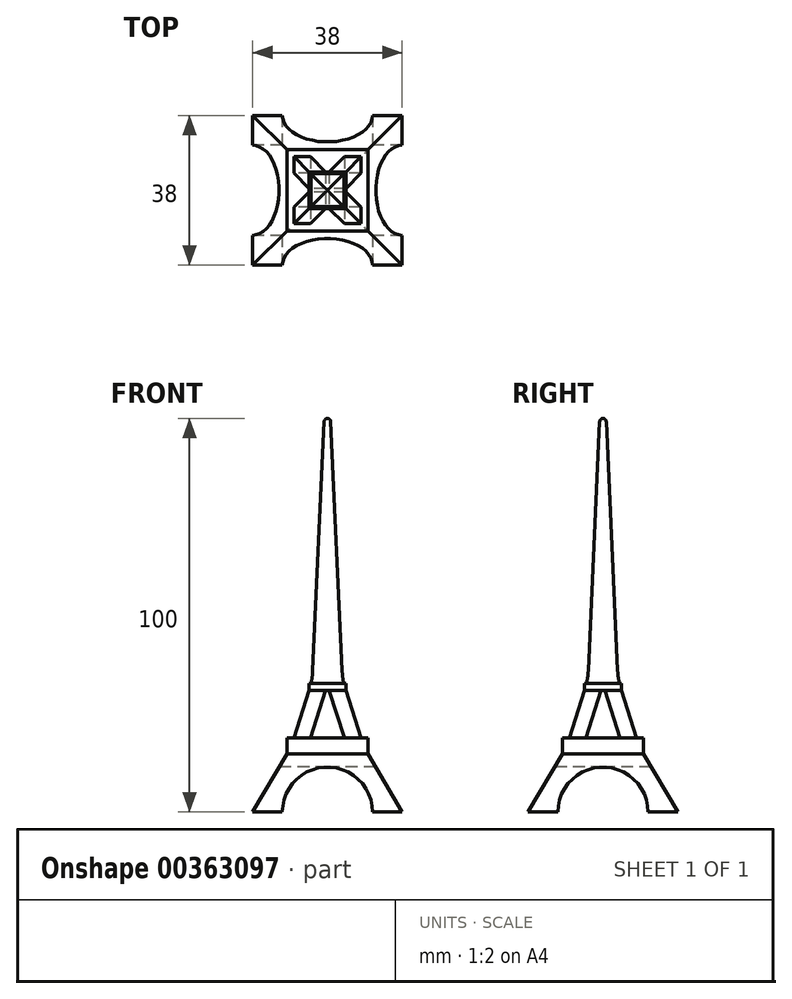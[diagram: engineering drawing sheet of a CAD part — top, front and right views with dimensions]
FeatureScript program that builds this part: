
annotation { "Feature Type Name" : "Feature", "Feature Type Description" : "" }
export const myFeature = defineFeature(function(context is Context, id is Id, definition is map)
    precondition{}
    {
        {
            var Q0;
            Q0=qCreatedBy(makeId("Front.planeOp"),FACE);
            var sketch = newSketch(context, id + "F0", { "sketchPlane" : qUnion([Q0])});
            skLineSegment(sketch, "E0.bottom", {"start": v(0, 0) * mm, "end": v(38, 0) * mm});
            skLineSegment(sketch, "E0.top", {"start": v(0, 100) * mm, "end": v(38, 100) * mm});
            skLineSegment(sketch, "E0.left", {"start": v(0, 0) * mm, "end": v(0, 100) * mm});
            skLineSegment(sketch, "E0.right", {"start": v(38, 0) * mm, "end": v(38, 100) * mm});
            skSolve(sketch);
        }
        {
            var Q0;
            Q0=makeQuery(id+"F0.imprint","IMPRINT",FACE,{"disambiguationData":[TD([[makeQuery(id+"F0.imprint","IMPRINT",EDGE,{"derivedFrom":sQuery(id+"F0.wireOp",EDGE,"E0.bottom")}),1.0]])]});
            extrude(context, id + "F1", {"entities" : qUnion([Q0]), "depth" : 38 * mm, "offsetDistance" : 25 * mm});
        }
        {
            var Q0;
            Q0=makeQuery(id+"F1.opExtrude","CAP_FACE",FACE,{"disambiguationData":[OSD([sQuery(id+"F0.wireOp",EDGE,"E0.bottom"),sQuery(id+"F0.wireOp",EDGE,"E0.top"),sQuery(id+"F0.wireOp",EDGE,"E0.left"),sQuery(id+"F0.wireOp",EDGE,"E0.right")])],"isStart":false});
            var sketch = newSketch(context, id + "F2", { "sketchPlane" : qUnion([Q0])});
            skPoint(sketch, "E1.endSnap0", {"position": v(19, 100) * mm});
            skLineSegment(sketch, "E2", {"start": v(19, 100) * mm, "end": v(19, 0) * mm, "construction": true});
            skLineSegment(sketch, "E3", {"start": v(19, 100) * mm, "end": v(19.03, 100) * mm});
            skLineSegment(sketch, "E4", {"start": v(19.83, 99.24) * mm, "end": v(22.72, 36.04) * mm});
            skLineSegment(sketch, "E5", {"start": v(38, 0) * mm, "end": v(29.32, 14.77) * mm});
            skLineSegment(sketch, "E6", {"start": v(27.53, 18.8) * mm, "end": v(23.66, 30.85) * mm});
            skArc(sketch, "E7", {"start": v(30.49, 0) * mm, "mid": v(27.12, 8.12) * mm, "end": v(19, 11.49) * mm});
            skLineSegment(sketch, "E8", {"start": v(38, 0) * mm, "end": v(30.49, 0) * mm});
            skPoint(sketch, "E9.visualSharp", {"position": v(22.85, 33.38) * mm});
            skArc(sketch, "E9.filletArc", {"start": v(22.72, 36.04) * mm, "mid": v(22.88, 34.33) * mm, "end": v(23.17, 32.64) * mm});
            skPoint(sketch, "E10.visualSharp", {"position": v(28.2, 16.68) * mm});
            skLineSegment(sketch, "E11.MirrorCS", {"start": v(18.17, 99.24) * mm, "end": v(15.28, 36.04) * mm});
            skArc(sketch, "E12.MirrorCS", {"start": v(15.28, 36.04) * mm, "mid": v(15.12, 34.33) * mm, "end": v(14.83, 32.64) * mm});
            skLineSegment(sketch, "E13.MirrorCS", {"start": v(10.47, 18.8) * mm, "end": v(14.34, 30.85) * mm});
            skLineSegment(sketch, "E14.MirrorCS", {"start": v(19, 100) * mm, "end": v(18.97, 100) * mm});
            skLineSegment(sketch, "E15.MirrorCS", {"start": v(0, 0) * mm, "end": v(8.68, 14.77) * mm});
            skArc(sketch, "E16.MirrorCS", {"start": v(7.51, 0) * mm, "mid": v(10.88, 8.12) * mm, "end": v(19, 11.49) * mm});
            skLineSegment(sketch, "E17.MirrorCS", {"start": v(0, 0) * mm, "end": v(7.51, 0) * mm});
            skLineSegment(sketch, "E18.bottom", {"start": v(-8.57, -4.89) * mm, "end": v(50.47, -4.89) * mm});
            skLineSegment(sketch, "E18.top", {"start": v(-8.57, 109.12) * mm, "end": v(50.47, 109.12) * mm});
            skLineSegment(sketch, "E18.left", {"start": v(-8.57, -4.89) * mm, "end": v(-8.57, 109.12) * mm});
            skLineSegment(sketch, "E18.right", {"start": v(50.47, -4.89) * mm, "end": v(50.47, 109.12) * mm});
            skLineSegment(sketch, "E19", {"start": v(29.32, 14.77) * mm, "end": v(29.32, 18.8) * mm});
            skLineSegment(sketch, "E20", {"start": v(29.32, 18.8) * mm, "end": v(27.53, 18.8) * mm});
            skLineSegment(sketch, "E21.MirrorCS", {"start": v(8.68, 18.8) * mm, "end": v(10.47, 18.8) * mm});
            skLineSegment(sketch, "E22.MirrorCS", {"start": v(8.68, 14.77) * mm, "end": v(8.68, 18.8) * mm});
            skLineSegment(sketch, "E23", {"start": v(23.66, 30.85) * mm, "end": v(23.66, 32.64) * mm});
            skLineSegment(sketch, "E24", {"start": v(23.66, 32.64) * mm, "end": v(23.17, 32.64) * mm});
            skLineSegment(sketch, "E25.MirrorCS", {"start": v(14.34, 30.85) * mm, "end": v(14.34, 32.64) * mm});
            skLineSegment(sketch, "E26.MirrorCS", {"start": v(14.34, 32.64) * mm, "end": v(14.83, 32.64) * mm});
            skPoint(sketch, "E27.orphan", {"position": v(14.34, 30.85) * mm});
            skPoint(sketch, "E28.visualSharp", {"position": v(18.2, 100) * mm});
            skArc(sketch, "E28.filletArc", {"start": v(18.97, 100) * mm, "mid": v(18.42, 99.78) * mm, "end": v(18.17, 99.24) * mm});
            skPoint(sketch, "E29.visualSharp", {"position": v(19.8, 100) * mm});
            skArc(sketch, "E29.filletArc", {"start": v(19.83, 99.24) * mm, "mid": v(19.58, 99.78) * mm, "end": v(19.03, 100) * mm});
            skLineSegment(sketch, "E30.0", {"start": v(14.67, 18.8) * mm, "end": v(18.54, 30.85) * mm});
            skLineSegment(sketch, "E31.0", {"start": v(23.33, 18.8) * mm, "end": v(19.46, 30.85) * mm});
            skLineSegment(sketch, "E32", {"start": v(23.33, 18.8) * mm, "end": v(14.67, 18.8) * mm});
            skLineSegment(sketch, "E33", {"start": v(19.46, 30.85) * mm, "end": v(18.54, 30.85) * mm});
            skSolve(sketch);
        }
        {
            var Q0;
            {var subQ2=sQuery(id+"F2.wireOp",EDGE,"E11.MirrorCS");Q0=makeQuery(id+"F2.imprint","IMPRINT",FACE,{"disambiguationData":[TD([[makeQuery(id+"F2.imprint","IMPRINT",EDGE,{"derivedFrom":subQ2}),-1.0]])]});}
            var Q1;
            {var subQ0=sQuery(id+"F2.wireOp",EDGE,"E7");Q1=makeQuery(id+"F2.imprint","IMPRINT",FACE,{"disambiguationData":[TD([[makeQuery(id+"F2.imprint","IMPRINT",EDGE,{"derivedFrom":subQ0}),1.0]])]});}
            var Q2;
            {var subQ2=sQuery(id+"F2.wireOp",EDGE,"E4");Q2=makeQuery(id+"F2.imprint","IMPRINT",FACE,{"disambiguationData":[TD([[makeQuery(id+"F2.imprint","IMPRINT",EDGE,{"derivedFrom":subQ2}),1.0]])]});}
            var Q3;
            Q3=makeQuery(id+"F2.imprint","IMPRINT",FACE,{"disambiguationData":[TD([[makeQuery(id+"F2.imprint","IMPRINT",EDGE,{"derivedFrom":sQuery(id+"F2.wireOp",EDGE,"E30.0")}),-1.0]])]});
            extrude(context, id + "F3", {"entities" : qUnion([Q0, Q1, Q2, Q3]), "operationType" : NewBodyOperationType.REMOVE, "endBound" : BoundingType.THROUGH_ALL, "oppositeDirection" : true, "depth" : 25 * mm});
        }
        {
            var Q0;
            Q0=qCreatedBy(makeId("Right.planeOp"),FACE);
            var sketch = newSketch(context, id + "F4", { "sketchPlane" : qUnion([Q0])});
            skPoint(sketch, "E34.endSnap0", {"position": v(-19, 100) * mm});
            skLineSegment(sketch, "E35", {"start": v(-19, 100) * mm, "end": v(-19, 0) * mm, "construction": true});
            skLineSegment(sketch, "E36", {"start": v(-19, 100) * mm, "end": v(-18.97, 100) * mm});
            skLineSegment(sketch, "E37", {"start": v(-18.17, 99.24) * mm, "end": v(-15.28, 36.04) * mm});
            skLineSegment(sketch, "E38", {"start": v(0, 0) * mm, "end": v(-8.68, 14.77) * mm});
            skLineSegment(sketch, "E39", {"start": v(-10.47, 18.8) * mm, "end": v(-14.34, 30.85) * mm});
            skArc(sketch, "E40", {"start": v(-7.51, 0) * mm, "mid": v(-10.88, 8.12) * mm, "end": v(-19, 11.49) * mm});
            skLineSegment(sketch, "E41", {"start": v(0, 0) * mm, "end": v(-7.51, 0) * mm});
            skPoint(sketch, "E42.visualSharp", {"position": v(-15.15, 33.38) * mm});
            skArc(sketch, "E42.filletArc", {"start": v(-15.28, 36.04) * mm, "mid": v(-15.12, 34.33) * mm, "end": v(-14.83, 32.64) * mm});
            skPoint(sketch, "E43.visualSharp", {"position": v(-9.8, 16.68) * mm});
            skLineSegment(sketch, "E44.MirrorCS", {"start": v(-19.83, 99.24) * mm, "end": v(-22.72, 36.04) * mm});
            skArc(sketch, "E45.MirrorCS", {"start": v(-22.72, 36.04) * mm, "mid": v(-22.88, 34.33) * mm, "end": v(-23.17, 32.64) * mm});
            skLineSegment(sketch, "E46.MirrorCS", {"start": v(-27.53, 18.8) * mm, "end": v(-23.66, 30.85) * mm});
            skLineSegment(sketch, "E47.MirrorCS", {"start": v(-19, 100) * mm, "end": v(-19.03, 100) * mm});
            skLineSegment(sketch, "E48.MirrorCS", {"start": v(-38, 0) * mm, "end": v(-29.32, 14.77) * mm});
            skArc(sketch, "E49.MirrorCS", {"start": v(-30.49, 0) * mm, "mid": v(-27.12, 8.12) * mm, "end": v(-19, 11.49) * mm});
            skLineSegment(sketch, "E50.MirrorCS", {"start": v(-38, 0) * mm, "end": v(-30.49, 0) * mm});
            skLineSegment(sketch, "E51.bottom", {"start": v(-46.57, -4.89) * mm, "end": v(12.47, -4.89) * mm});
            skLineSegment(sketch, "E51.top", {"start": v(-46.57, 109.12) * mm, "end": v(12.47, 109.12) * mm});
            skLineSegment(sketch, "E51.left", {"start": v(-46.57, -4.89) * mm, "end": v(-46.57, 109.12) * mm});
            skLineSegment(sketch, "E51.right", {"start": v(12.47, -4.89) * mm, "end": v(12.47, 109.12) * mm});
            skLineSegment(sketch, "E52", {"start": v(-8.68, 14.77) * mm, "end": v(-8.68, 18.8) * mm});
            skLineSegment(sketch, "E53", {"start": v(-8.68, 18.8) * mm, "end": v(-10.47, 18.8) * mm});
            skLineSegment(sketch, "E54.MirrorCS", {"start": v(-29.32, 18.8) * mm, "end": v(-27.53, 18.8) * mm});
            skLineSegment(sketch, "E55.MirrorCS", {"start": v(-29.32, 14.77) * mm, "end": v(-29.32, 18.8) * mm});
            skLineSegment(sketch, "E56", {"start": v(-14.34, 30.85) * mm, "end": v(-14.34, 32.64) * mm});
            skLineSegment(sketch, "E57", {"start": v(-14.34, 32.64) * mm, "end": v(-14.83, 32.64) * mm});
            skLineSegment(sketch, "E58.MirrorCS", {"start": v(-23.66, 30.85) * mm, "end": v(-23.66, 32.64) * mm});
            skLineSegment(sketch, "E59.MirrorCS", {"start": v(-23.66, 32.64) * mm, "end": v(-23.17, 32.64) * mm});
            skPoint(sketch, "E60.MirrorCS.center.orphan", {"position": v(-46.57, 24.9) * mm});
            skPoint(sketch, "E60.MirrorCS.start.orphan", {"position": v(-27.53, 18.8) * mm});
            skPoint(sketch, "E61.orphan", {"position": v(-23.66, 30.85) * mm});
            skLineSegment(sketch, "E62.0", {"start": v(-23.33, 18.8) * mm, "end": v(-19.46, 30.85) * mm});
            skLineSegment(sketch, "E63.0", {"start": v(-14.67, 18.8) * mm, "end": v(-18.54, 30.85) * mm});
            skLineSegment(sketch, "E64", {"start": v(-14.67, 18.8) * mm, "end": v(-23.33, 18.8) * mm});
            skLineSegment(sketch, "E65", {"start": v(-14.34, 30.85) * mm, "end": v(-23.66, 30.85) * mm});
            skPoint(sketch, "E66.visualSharp", {"position": v(-19.8, 100) * mm});
            skArc(sketch, "E66.filletArc", {"start": v(-19.03, 100) * mm, "mid": v(-19.58, 99.78) * mm, "end": v(-19.83, 99.24) * mm});
            skPoint(sketch, "E67.visualSharp", {"position": v(-18.2, 100) * mm});
            skArc(sketch, "E67.filletArc", {"start": v(-18.17, 99.24) * mm, "mid": v(-18.42, 99.78) * mm, "end": v(-18.97, 100) * mm});
            skSolve(sketch);
        }
        {
            var Q0;
            Q0=makeQuery(id+"F4.imprint","IMPRINT",FACE,{"disambiguationData":[TD([[makeQuery(id+"F4.imprint","IMPRINT",EDGE,{"derivedFrom":sQuery(id+"F4.wireOp",EDGE,"E36")}),1.0]])]});
            var Q1;
            Q1=makeQuery(id+"F4.imprint","IMPRINT",FACE,{"disambiguationData":[TD([[makeQuery(id+"F4.imprint","IMPRINT",EDGE,{"derivedFrom":sQuery(id+"F4.wireOp",EDGE,"E62.0")}),-1.0]])]});
            extrude(context, id + "F5", {"entities" : qUnion([Q0, Q1]), "operationType" : NewBodyOperationType.REMOVE, "endBound" : BoundingType.THROUGH_ALL, "depth" : 25 * mm});
        }
    });
